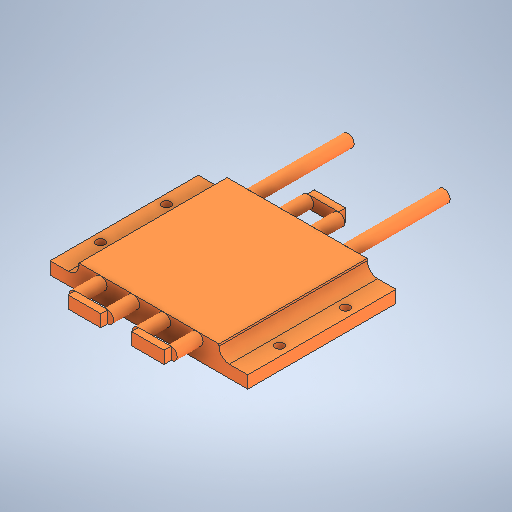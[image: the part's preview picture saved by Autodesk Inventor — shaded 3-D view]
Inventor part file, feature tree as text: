
AUTODESK INVENTOR PART (.ipt)
format: ipt  version: 2025.2 (Build 292293000, 293)  size: 377,344 bytes
history: native  units: mm
features: extrude x9, sketch x9, fillet x2, plane x1, mirror x1
ambient origin geometry x8: Origin, YZ Plane, XZ Plane, XY Plane, X Axis, Y Axis, Z Axis, Center Point
bodies: Solid1 (feature_tree)
feature tree (22):
  extrude  "Extrusion1"  Depth=114.3mm
  extrude  "Extrusion2"  Depth=108.0mm
  fillet  "Fillet1"  Radius=114.3mm
  fillet  "Fillet2"  Radius=9.55mm
  extrude  "Extrusion3"  Depth=8.0mm
  extrude  "Extrusion4"  Depth=9.55mm
  extrude  "Extrusion5"  Depth=9.525mm
  extrude  "Extrusion6"  Depth=9.525mm
  extrude  "Extrusion7"  Depth=9.525mm
  extrude  "Extrusion8"  Depth=25.0mm
  extrude  "Extrusion9"  Depth=20.0mm TaperAngle=0.0deg
  plane  "Work Plane1"
  mirror  "Mirror1"
  sketch  "Sketch1"  dims[d0=152.4mm d1=114.3mm]
  sketch  "Sketch2"  dims[d2=9.55mm d3=0.0mm d4=108.0mm d5=114.3mm d6=9.55mm d7=0.0mm]
  sketch  "Sketch3"  dims[d8=8.0mm d9=8.0mm]
  sketch  "Sketch4"  dims[d10=9.55mm d11=4.775mm]
  sketch  "Sketch5"  dims[d12=152.4mm d13=9.525mm]
  sketch  "Sketch6"  dims[d14=9.525mm d15=9.525mm]
  sketch  "Sketch7"  dims[d16=9.525mm d17=25.0mm]
  sketch  "Sketch8"  dims[d18=25.0mm d19=25.0mm]
  sketch  "Sketch9"  dims[d20=25.0mm d21=20.0mm d22=0.0mm d23=5.4mm d24=0.0mm d25=5.4mm d26=0.0mm d27=76.2mm d28=0.0mm d29=20.0mm d30=0.0mm d31=5.4mm d32=0.0mm d36=25.4mm d37=25.4mm d38=6.73mm d39=6.73mm d40=10.0mm d41=0.0mm d42=39.2mm d43=39.2mm d44=74.0mm d45=23.76338mm d46=25.021416mm]
